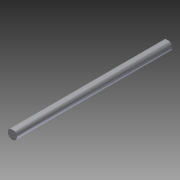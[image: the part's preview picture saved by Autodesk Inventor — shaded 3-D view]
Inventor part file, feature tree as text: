
AUTODESK INVENTOR PART (.ipt)
format: ipt  version: 2012 (Build 160160000, 160)  size: 84,992 bytes
history: native  units: in
note: dims shown in document units (in); Inventor stores cm internally (conversion verified against a paired STEP export)
features: imported_body x1, extrude x1, sketch x1
ambient origin geometry x8: Origin, YZ Plane, XZ Plane, XY Plane, X Axis, Y Axis, Z Axis, Center Point
bodies: Solid1 (feature_tree)
feature tree (3):
  imported_body  "Base1"
  extrude  "Extrusion1"  [1 undecoded]
  sketch  "Sketch1"  dims[d0=0.782in d1=0.0in]
note: 1 required parameter value undecoded (feature->parameter linkage not recoverable at this tier; creation-order binding heuristic only, values carry confidence <= 0.55)
